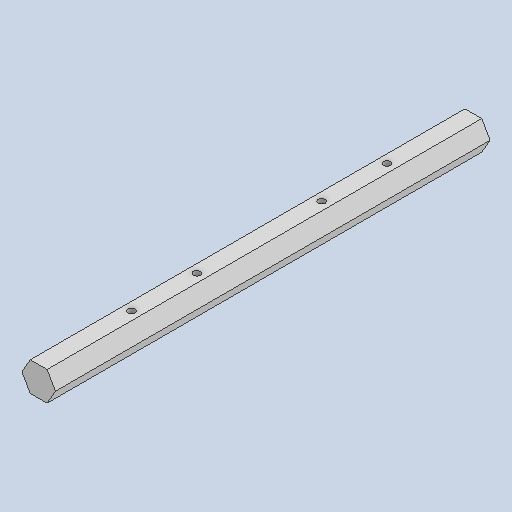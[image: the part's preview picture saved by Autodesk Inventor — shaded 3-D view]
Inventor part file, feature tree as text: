
AUTODESK INVENTOR PART (.ipt)
format: ipt  version: 2022 (Build 260153000, 153)  size: 122,880 bytes
history: native  units: mm
features: extrude x2, sketch x2
ambient origin geometry x8: Origin, YZ Plane, XZ Plane, XY Plane, X Axis, Y Axis, Z Axis, Center Point
bodies: Body1 (feature_tree)
feature tree (4):
  extrude  "Extrusion5"  Depth=3.1mm TaperAngle=360.0deg
  extrude  "Extrusion6"  Depth=80.0mm
  sketch  "Sketch4"  dims[d15=3.1mm d16=60.0mm d18=360.0deg]
  sketch  "Sketch5"  dims[d20=80.0mm d21=0.0mm d22=1.3mm d23=64.1mm d24=52.1mm d25=29.1mm d26=17.1mm d27=6.0mm d28=0.0mm]
